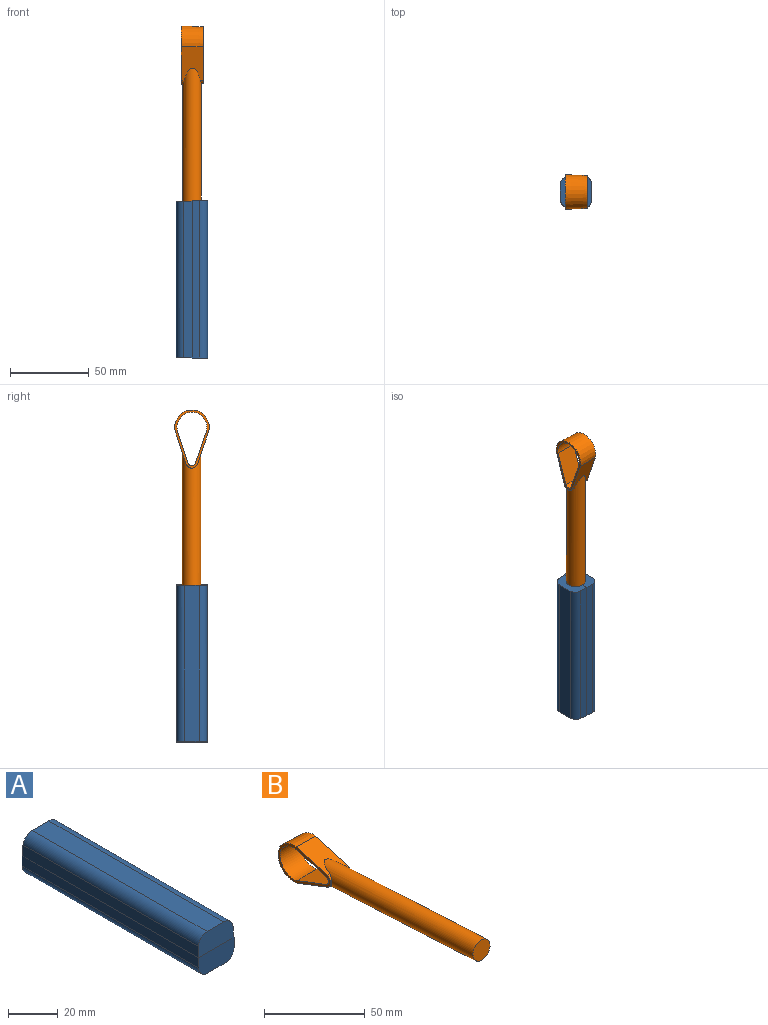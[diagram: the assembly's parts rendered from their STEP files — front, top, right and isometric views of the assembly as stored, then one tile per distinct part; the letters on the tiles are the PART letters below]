
ASSEMBLY  parts=2 mates=1
PART A: 16 faces, bbox 20x100x20 mm
  f0: plane 20x10mm, normal (0,1,0), area 132.7mm2, adj f3,f6,f7,f8,f10,f11,f14
  f1: plane 20x10mm, normal (0,-1,0.05), area 185.5mm2, adj f2,f4,f5,f9,f12,f13
  f2: plane 100x5.26mm, normal (1,0,0.05), area 525.4mm2, adj f1,f3,f8,f12
  f3: plane 20x10mm, normal (0,1,0.05), area 128.9mm2, adj f0,f2,f4,f5,f12,f13,f14
  f4: plane 100x5.26mm, normal (-1,0,0.05), area 525.4mm2, adj f1,f3,f7,f13
  f5: plane 98.95x9.46mm, normal (0,0,1), area 936.3mm2, adj f1,f3,f12,f13
  f6: plane 100x10mm, normal (0,0,-1), area 1000mm2, adj f0,f9,f10,f11
  f7: plane 100x5mm, normal (-1,0,0), area 500mm2, adj f0,f4,f9,f11
  f8: plane 100x5mm, normal (1,0,0), area 500mm2, adj f0,f2,f9,f10
  f9: plane 20x10mm, normal (0,-1,0), area 189.3mm2, adj f1,f6,f7,f8,f10,f11
  f10: cylinder r=5mm len=100mm, axis (0,-1,0), area 785.4mm2, adj f0,f6,f8,f9
  f11: cylinder r=5mm len=100mm, axis (0,-1,0), area 785.4mm2, adj f0,f6,f7,f9
  f12: cylinder r=5mm len=99.45mm, axis (0,1,0), area 752.6mm2, adj f1,f2,f3,f5
  f13: cylinder r=5mm len=99.45mm, axis (0,1,0), area 752.6mm2, adj f1,f3,f4,f5
  f14: cylinder r=6mm len=25mm, axis (0,1,0), area 938.7mm2, adj f0,f3,f15
  f15: plane 12x12mm, normal (0,1,0), area 113.1mm2, adj f14
PART B: 13 faces, bbox 14x136.6x23.4 mm
  f0: plane 22.09x14mm, normal (0.03,-0.27,0.96), area 260.2mm2, adj f1,f2,f4,f5,f6,f11
  f1: cone r=4mm half-angle=2deg, axis (-1,0,0), area 11.9mm2, adj f0,f3,f4,f11
  f2: cone r=4mm half-angle=2deg, axis (-1,0,0), area 10.6mm2, adj f0,f3,f5,f11
  f3: plane 21.28x14mm, normal (0.03,-0.36,-0.93), area 257.6mm2, adj f1,f2,f4,f5,f6,f11
  f4: plane 36.02x21.02mm, normal (1,0,0), area 83mm2, adj f0,f1,f3,f6,f7,f8,f9,f10
  f5: plane 37x22mm, normal (-1,0,0), area 127.9mm2, adj f0,f2,f3,f6,f7,f8,f9,f10
  f6: cone r=11mm half-angle=2deg, axis (-1,0,0), area 536.3mm2, adj f0,f3,f4,f5
  f7: plane 21.78x14mm, normal (0,0.27,-0.96), area 317mm2, adj f4,f5,f8,f10
  f8: cylinder r=2.56mm len=14mm, axis (1,0,0), area 75.3mm2, adj f4,f5,f7,f9
  f9: plane 20.94x14mm, normal (0,0.36,0.93), area 314.1mm2, adj f4,f5,f8,f10
  f10: cylinder r=9.56mm len=19.12mm, axis (1,0,0), area 474.6mm2, adj f4,f5,f7,f9
  f11: cylinder r=6mm len=110.21mm, axis (0,-1,0.05), area 3936.8mm2, adj f0,f1,f2,f3,f12
  f12: plane 12x11.98mm, normal (0,-1,0.05), area 113.1mm2, adj f11
PLACE A rot(axis=(0.58,-0.58,-0.58),120deg) t=(-158.78,-18.19,-0.6)mm
PLACE B rot(axis=(1,0,0),93deg) t=(-165.57,44.96,249.4)mm
MATE fastened B.f11 <-> A.f14  axis (0,0,-1) through (-158.78,-8.19,74.4)mm
